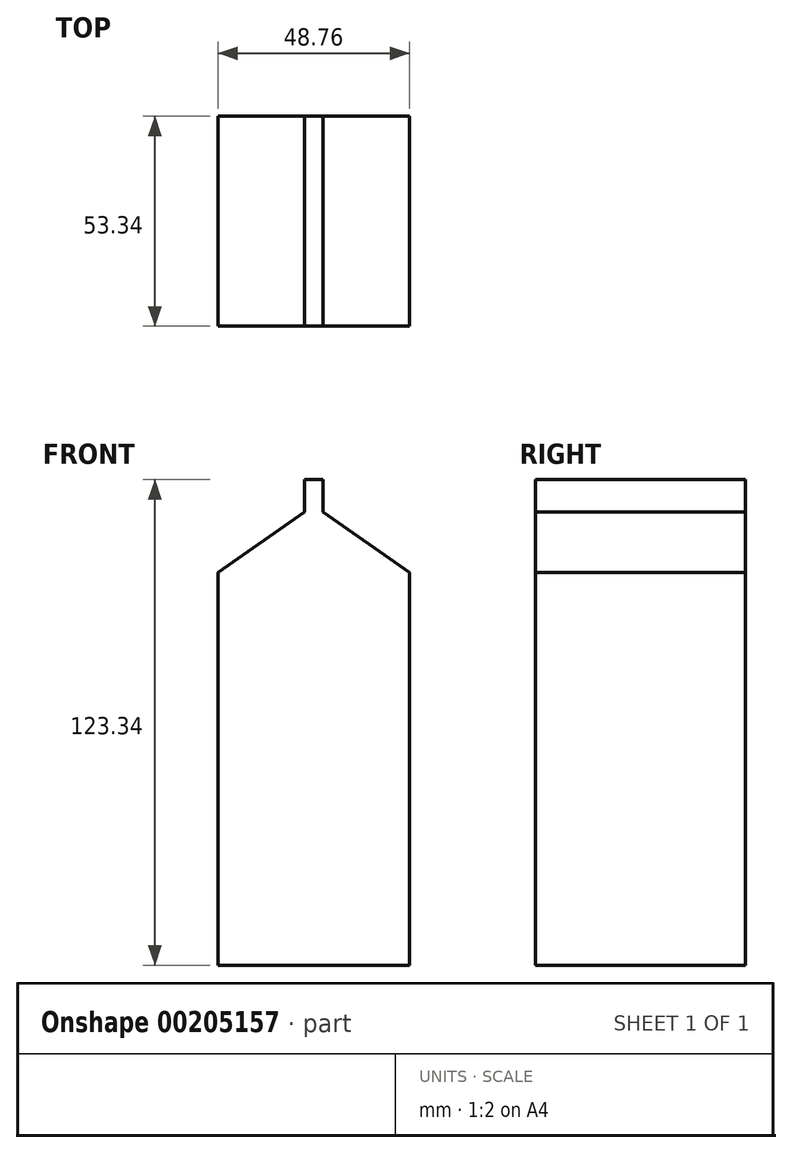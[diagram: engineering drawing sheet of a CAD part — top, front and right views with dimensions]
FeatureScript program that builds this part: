
annotation { "Feature Type Name" : "Feature", "Feature Type Description" : "" }
export const myFeature = defineFeature(function(context is Context, id is Id, definition is map)
    precondition{}
    {
        {
            var Q0;
            Q0=qCreatedBy(makeId("Front.planeOp"),FACE);
            var sketch = newSketch(context, id + "F0", { "sketchPlane" : qUnion([Q0])});
            skLineSegment(sketch, "E0.bottom", {"start": v(24.38, 49.86) * mm, "end": v(-24.38, 49.86) * mm});
            skLineSegment(sketch, "E0.top", {"start": v(24.38, -49.86) * mm, "end": v(-24.38, -49.86) * mm});
            skLineSegment(sketch, "E0.left", {"start": v(24.38, 49.86) * mm, "end": v(24.38, -49.86) * mm});
            skLineSegment(sketch, "E0.right", {"start": v(-24.38, 49.86) * mm, "end": v(-24.38, -49.86) * mm});
            skPoint(sketch, "E0.middle", {"position": v(0, 0) * mm});
            skLineSegment(sketch, "E1", {"start": v(24.38, 49.86) * mm, "end": v(2.33, 65.24) * mm});
            skLineSegment(sketch, "E2", {"start": v(2.33, 65.24) * mm, "end": v(2.33, 73.48) * mm});
            skLineSegment(sketch, "E3", {"start": v(2.33, 73.48) * mm, "end": v(0, 73.48) * mm});
            skLineSegment(sketch, "E4.MirrorCS", {"start": v(-2.33, 73.48) * mm, "end": v(0, 73.48) * mm});
            skLineSegment(sketch, "E5.MirrorCS", {"start": v(-2.33, 65.24) * mm, "end": v(-2.33, 73.48) * mm});
            skLineSegment(sketch, "E6.MirrorCS", {"start": v(-24.38, 49.86) * mm, "end": v(-2.33, 65.24) * mm});
            skSolve(sketch);
        }
        {
            var Q0;
            Q0=makeQuery(id+"F0.imprint","IMPRINT",FACE,{"disambiguationData":[TD([[makeQuery(id+"F0.imprint","IMPRINT",EDGE,{"derivedFrom":sQuery(id+"F0.wireOp",EDGE,"E0.bottom")}),1.0]])]});
            var Q1;
            Q1=makeQuery(id+"F0.imprint","IMPRINT",FACE,{"disambiguationData":[TD([[makeQuery(id+"F0.imprint","IMPRINT",EDGE,{"derivedFrom":sQuery(id+"F0.wireOp",EDGE,"E0.bottom")}),-1.0]])]});
            extrude(context, id + "F1", {"entities" : qUnion([Q0, Q1]), "endBound" : BoundingType.SYMMETRIC, "depth" : 53.34 * mm});
        }
    });
